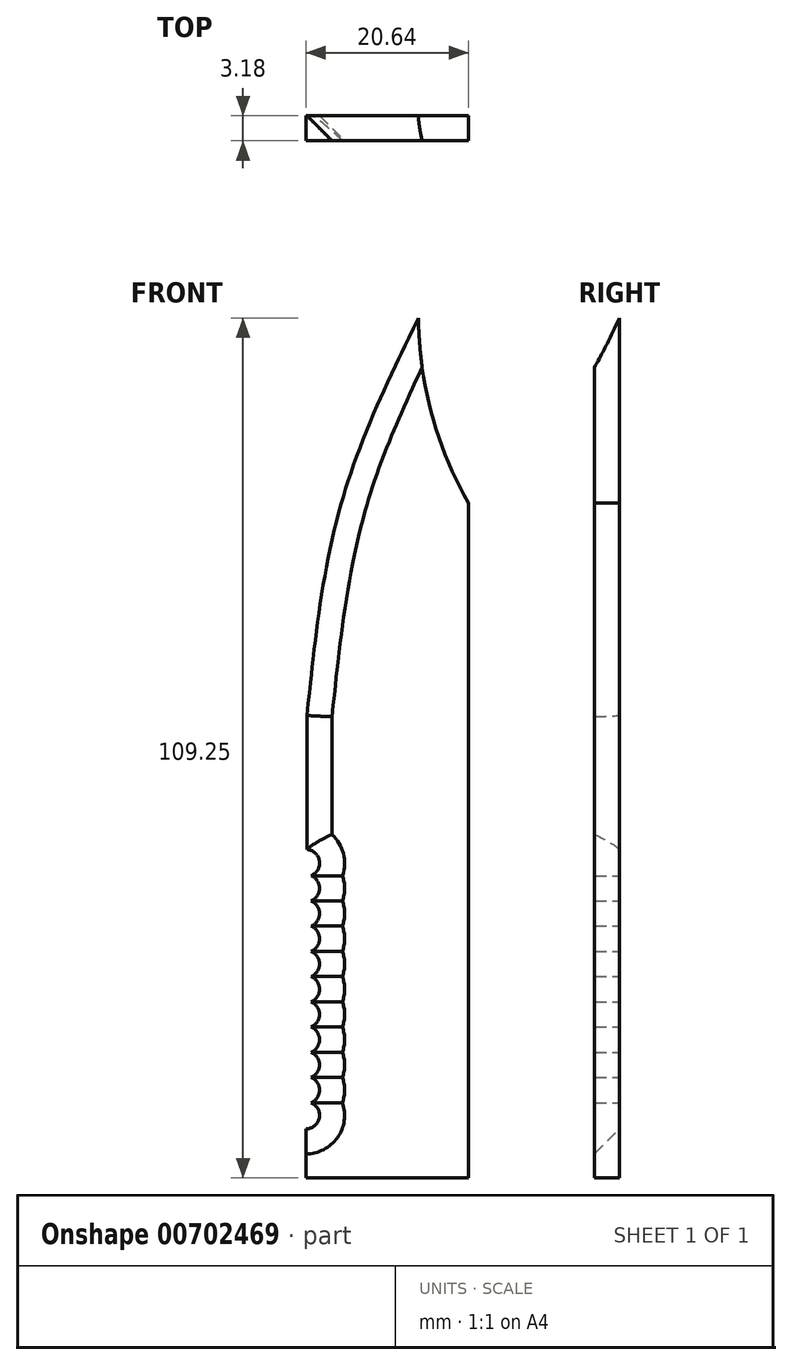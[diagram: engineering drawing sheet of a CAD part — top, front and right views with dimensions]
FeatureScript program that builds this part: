
annotation { "Feature Type Name" : "Feature", "Feature Type Description" : "" }
export const myFeature = defineFeature(function(context is Context, id is Id, definition is map)
    precondition{}
    {
        {
            var Q0;
            Q0=qCreatedBy(makeId("Front.planeOp"),FACE);
            var sketch = newSketch(context, id + "F0", { "sketchPlane" : qUnion([Q0])});
            skLineSegment(sketch, "E0", {"start": v(0, 0) * mm, "end": v(20.64, 0) * mm});
            skLineSegment(sketch, "E1", {"start": v(20.64, 0) * mm, "end": v(20.64, 85.73) * mm});
            skLineSegment(sketch, "E2", {"start": v(20.64, 85.73) * mm, "end": v(20.64, 109.54) * mm});
            skLineSegment(sketch, "E3", {"start": v(20.64, 109.54) * mm, "end": v(14.29, 109.54) * mm});
            skLineSegment(sketch, "E4", {"start": v(14.29, 109.54) * mm, "end": v(20.64, 85.73) * mm});
            skLineSegment(sketch, "E5", {"start": v(17.46, 97.63) * mm, "end": v(15.93, 97.22) * mm});
            skArc(sketch, "E6", {"start": v(14.29, 109.54) * mm, "mid": v(15.93, 97.22) * mm, "end": v(20.64, 85.73) * mm});
            skLineSegment(sketch, "E7", {"start": v(14.29, 109.54) * mm, "end": v(0, 109.54) * mm});
            skLineSegment(sketch, "E8", {"start": v(0, 109.54) * mm, "end": v(0, 58.74) * mm});
            skLineSegment(sketch, "E9", {"start": v(0, 58.74) * mm, "end": v(14.29, 109.54) * mm});
            skLineSegment(sketch, "E10", {"start": v(7.14, 84.14) * mm, "end": v(4.33, 85.61) * mm});
            skFitSpline(sketch, "E11", {"points": [v(14.29, 109.54) * mm, v(4.33, 85.61) * mm, v(0, 58.74) * mm], "startDerivative": vector(-23.02, -47.3) * mm, "endDerivative": vector(-5.63, -54.28) * mm});
            skLineSegment(sketch, "E12", {"start": v(0, 58.74) * mm, "end": v(0, 41.58) * mm});
            skLineSegment(sketch, "E13", {"start": v(0, 0) * mm, "end": v(0, 1.26) * mm});
            skPoint(sketch, "E14.orphan", {"position": v(-2.28, 6.32) * mm});
            skLineSegment(sketch, "E15", {"start": v(20.64, 6.34) * mm, "end": v(0, 6.34) * mm});
            skPoint(sketch, "E16.MirrorCS.end.orphan", {"position": v(-1.12, 5.06) * mm});
            skPoint(sketch, "E16.MirrorCS.start.orphan", {"position": v(-1.12, 6.32) * mm});
            skPoint(sketch, "E17.orphan", {"position": v(-0.35, 5.06) * mm});
            skPoint(sketch, "E18.orphan", {"position": v(-2.28, 0) * mm});
            skPoint(sketch, "E19.MirrorCS.start.orphan", {"position": v(-1.12, 3.8) * mm});
            skPoint(sketch, "E20.end.orphan", {"position": v(-2.5, 0) * mm});
            skPoint(sketch, "E20.start.orphan", {"position": v(-2.5, 5.06) * mm});
            skPoint(sketch, "E21.MirrorCS.end.orphan", {"position": v(-1.12, 2.53) * mm});
            skPoint(sketch, "E22.orphan", {"position": v(-0.53, 2.53) * mm});
            skPoint(sketch, "E23.start.orphan", {"position": v(-1.71, 2.53) * mm});
            skPoint(sketch, "E24.MirrorCS.end.orphan", {"position": v(-1.12, 0) * mm});
            skPoint(sketch, "E24.MirrorCS.start.orphan", {"position": v(-1.12, 1.26) * mm});
            skPoint(sketch, "E25.orphan", {"position": v(-0.53, 1.26) * mm});
            skPoint(sketch, "E26.MirrorCS.start.orphan", {"position": v(-1.71, 1.26) * mm});
            skPoint(sketch, "E27.start.orphan", {"position": v(-1.9, 6.34) * mm});
            skPoint(sketch, "E28.end.orphan", {"position": v(-0.11, 6.34) * mm});
            skPoint(sketch, "E29.start.orphan", {"position": v(-2.28, 6.34) * mm});
            skPoint(sketch, "E30.MirrorCS.end.orphan", {"position": v(-0.43, 9.4) * mm});
            skPoint(sketch, "E30.MirrorCS.start.orphan", {"position": v(-0.43, 7.87) * mm});
            skPoint(sketch, "E31.orphan", {"position": v(-0.16, 7.87) * mm});
            skPoint(sketch, "E32.start.orphan", {"position": v(-0.17, 7.1) * mm});
            skPoint(sketch, "E33.orphan", {"position": v(-0.17, 6.72) * mm});
            skLineSegment(sketch, "E34", {"start": v(-0.6, 6.46) * mm, "end": v(-0.6, 6.34) * mm});
            skPoint(sketch, "E35.MirrorCS.start.orphan", {"position": v(0, 7.87) * mm});
            skPoint(sketch, "E36.MirrorCS.start.orphan", {"position": v(0, 7.1) * mm});
            skPoint(sketch, "E37.end.orphan", {"position": v(0, 6.72) * mm});
            skLineSegment(sketch, "E38", {"start": v(0, 7.94) * mm, "end": v(0, 7.87) * mm});
            skArc(sketch, "E39", {"start": v(-0.6, 6.46) * mm, "mid": v(1.57, 7.64) * mm, "end": v(0, 9.54) * mm});
            skPoint(sketch, "E40.orphan", {"position": v(-0.6, 7.94) * mm});
            skLineSegment(sketch, "E41.trimOffspring", {"start": v(-0.43, 6.4) * mm, "end": v(-0.43, 6.34) * mm});
            skPoint(sketch, "E42.start.orphan", {"position": v(-0.43, 7.94) * mm});
            skLineSegment(sketch, "E43.trimOffspring", {"start": v(0, 6.34) * mm, "end": v(0, 0) * mm});
            skPoint(sketch, "E44", {"position": v(-0.31, 8.58) * mm});
            skPoint(sketch, "E45", {"position": v(-1.08, 8.14) * mm});
            skPoint(sketch, "E46", {"position": v(-0.43, 7.23) * mm});
            skPoint(sketch, "E47", {"position": v(-0.43, 7.47) * mm});
            skPoint(sketch, "E48", {"position": v(-0.6, 7.47) * mm});
            skPoint(sketch, "E49", {"position": v(-1.03, 7.65) * mm});
            skPoint(sketch, "E50", {"position": v(-0.73, 8.63) * mm});
            skPoint(sketch, "E51", {"position": v(0.7, 8.48) * mm});
            skPoint(sketch, "E52", {"position": v(0.5, 7.67) * mm});
            skPoint(sketch, "E53", {"position": v(0.8, 8.03) * mm});
            skPoint(sketch, "E54", {"position": v(0.37, 8.36) * mm});
            skPoint(sketch, "E55", {"position": v(0.37, 8.03) * mm});
            skPoint(sketch, "E56", {"position": v(0.64, 6.96) * mm});
            skPoint(sketch, "E57", {"position": v(0.8, 7.66) * mm});
            skPoint(sketch, "E58", {"position": v(0.26, 7.26) * mm});
            skPoint(sketch, "E59", {"position": v(0, 7.58) * mm});
            skPoint(sketch, "E60", {"position": v(-0.6, 10.6) * mm});
            skArc(sketch, "E61.MirrorC", {"start": v(0, 12.75) * mm, "mid": v(1.6, 11.15) * mm, "end": v(0, 9.54) * mm});
            skArc(sketch, "E62.MirrorC", {"start": v(0, 12.75) * mm, "mid": v(1.6, 14.35) * mm, "end": v(0, 15.95) * mm});
            skArc(sketch, "E63.MirrorC", {"start": v(0, 19.16) * mm, "mid": v(1.6, 17.55) * mm, "end": v(0, 15.95) * mm});
            skArc(sketch, "E64.MirrorC", {"start": v(0, 19.16) * mm, "mid": v(1.6, 20.76) * mm, "end": v(0, 22.36) * mm});
            skArc(sketch, "E65.MirrorC", {"start": v(0, 25.56) * mm, "mid": v(1.6, 23.96) * mm, "end": v(0, 22.36) * mm});
            skArc(sketch, "E66.MirrorC", {"start": v(0, 25.56) * mm, "mid": v(1.6, 27.17) * mm, "end": v(0, 28.77) * mm});
            skArc(sketch, "E67.MirrorC", {"start": v(0, 31.97) * mm, "mid": v(1.6, 30.37) * mm, "end": v(0, 28.77) * mm});
            skArc(sketch, "E68.MirrorC", {"start": v(0, 31.97) * mm, "mid": v(1.6, 33.57) * mm, "end": v(0, 35.17) * mm});
            skArc(sketch, "E69.MirrorC", {"start": v(0, 38.38) * mm, "mid": v(1.6, 36.78) * mm, "end": v(0, 35.17) * mm});
            skArc(sketch, "E70.MirrorC", {"start": v(0, 38.38) * mm, "mid": v(1.6, 39.98) * mm, "end": v(0, 41.58) * mm});
            skPoint(sketch, "E71.start.orphan", {"position": v(0, 19.16) * mm});
            skPoint(sketch, "E72.orphan", {"position": v(1.8, 9.54) * mm});
            skPoint(sketch, "E73.orphan", {"position": v(0, 9.54) * mm});
            skSolve(sketch);
        }
        {
            var Q0;
            {var subQ5=sQuery(id+"F0.wireOp",EDGE,"E15");Q0=makeQuery(id+"F0.imprint","IMPRINT",FACE,{"disambiguationData":[TD([[makeQuery(id+"F0.imprint","IMPRINT",EDGE,{"derivedFrom":subQ5}),-1.0]])]});}
            var Q1;
            {var subQ4=sQuery(id+"F0.wireOp",EDGE,"E0");Q1=makeQuery(id+"F0.imprint","IMPRINT",FACE,{"disambiguationData":[TD([[makeQuery(id+"F0.imprint","IMPRINT",EDGE,{"derivedFrom":subQ4}),1.0]])]});}
            var Q2;
            {var subQ3=sQuery(id+"F0.wireOp",EDGE,"E10");Q2=makeQuery(id+"F0.imprint","IMPRINT",FACE,{"disambiguationData":[TD([[makeQuery(id+"F0.imprint","IMPRINT",EDGE,{"derivedFrom":subQ3}),-1.0]])]});}
            var Q3;
            {var subQ3=sQuery(id+"F0.wireOp",EDGE,"E10");Q3=makeQuery(id+"F0.imprint","IMPRINT",FACE,{"disambiguationData":[TD([[makeQuery(id+"F0.imprint","IMPRINT",EDGE,{"derivedFrom":subQ3}),1.0]])]});}
            extrude(context, id + "F1", {"entities" : qUnion([Q0, Q1, Q2, Q3]), "depth" : 3.17 * mm, "offsetDistance" : 25.4 * mm});
        }
        {
            var Q0;
            Q0=makeQuery(id+"F1.opExtrude","CAP_EDGE",EDGE,{"disambiguationData":[OSD([sQuery(id+"F0.wireOp",EDGE,"E61.MirrorC")])],"isStart":false});
            var Q1;
            Q1=makeQuery(id+"F1.opExtrude","CAP_EDGE",EDGE,{"disambiguationData":[OSD([sQuery(id+"F0.wireOp",EDGE,"E68.MirrorC")])],"isStart":false});
            var Q2;
            Q2=makeQuery(id+"F1.opExtrude","CAP_EDGE",EDGE,{"disambiguationData":[OSD([sQuery(id+"F0.wireOp",EDGE,"E67.MirrorC")])],"isStart":false});
            var Q3;
            Q3=makeQuery(id+"F1.opExtrude","CAP_EDGE",EDGE,{"disambiguationData":[OSD([sQuery(id+"F0.wireOp",EDGE,"E65.MirrorC")])],"isStart":false});
            var Q4;
            Q4=makeQuery(id+"F1.opExtrude","CAP_EDGE",EDGE,{"disambiguationData":[OSD([sQuery(id+"F0.wireOp",EDGE,"E66.MirrorC")])],"isStart":false});
            var Q5;
            Q5=makeQuery(id+"F1.opExtrude","CAP_EDGE",EDGE,{"disambiguationData":[OSD([sQuery(id+"F0.wireOp",EDGE,"E69.MirrorC")])],"isStart":false});
            var Q6;
            Q6=makeQuery(id+"F1.opExtrude","CAP_EDGE",EDGE,{"disambiguationData":[OSD([sQuery(id+"F0.wireOp",EDGE,"E70.MirrorC")])],"isStart":false});
            var Q7;
            Q7=makeQuery(id+"F1.opExtrude","CAP_EDGE",EDGE,{"disambiguationData":[OSD([sQuery(id+"F0.wireOp",EDGE,"E64.MirrorC")])],"isStart":false});
            var Q8;
            Q8=makeQuery(id+"F1.opExtrude","CAP_EDGE",EDGE,{"disambiguationData":[OSD([sQuery(id+"F0.wireOp",EDGE,"E63.MirrorC")])],"isStart":false});
            var Q9;
            Q9=makeQuery(id+"F1.opExtrude","CAP_EDGE",EDGE,{"disambiguationData":[OSD([sQuery(id+"F0.wireOp",EDGE,"E62.MirrorC")])],"isStart":false});
            var Q10;
            Q10=makeQuery(id+"F1.opExtrude","CAP_EDGE",EDGE,{"disambiguationData":[OSD([sQuery(id+"F0.wireOp",EDGE,"E39")])],"isStart":false});
            chamfer(context, id + "F2", {"entities" : qUnion([Q0, Q1, Q2, Q3, Q4, Q5, Q6, Q7, Q8, Q9, Q10]), "width" : 3.3 * mm, "tangentPropagation" : true});
        }
        {
            var Q0;
            Q0=makeQuery(id+"F1.opExtrude","CAP_EDGE",EDGE,{"disambiguationData":[OSD([sQuery(id+"F0.wireOp",EDGE,"E12")])],"isStart":false});
            var Q1;
            Q1=makeQuery(id+"F1.opExtrude","CAP_EDGE",EDGE,{"disambiguationData":[OSD([sQuery(id+"F0.wireOp",EDGE,"E11")])],"isStart":false});
            chamfer(context, id + "F3", {"entities" : qUnion([Q0, Q1]), "width" : 3.3 * mm, "tangentPropagation" : true});
        }
    });
